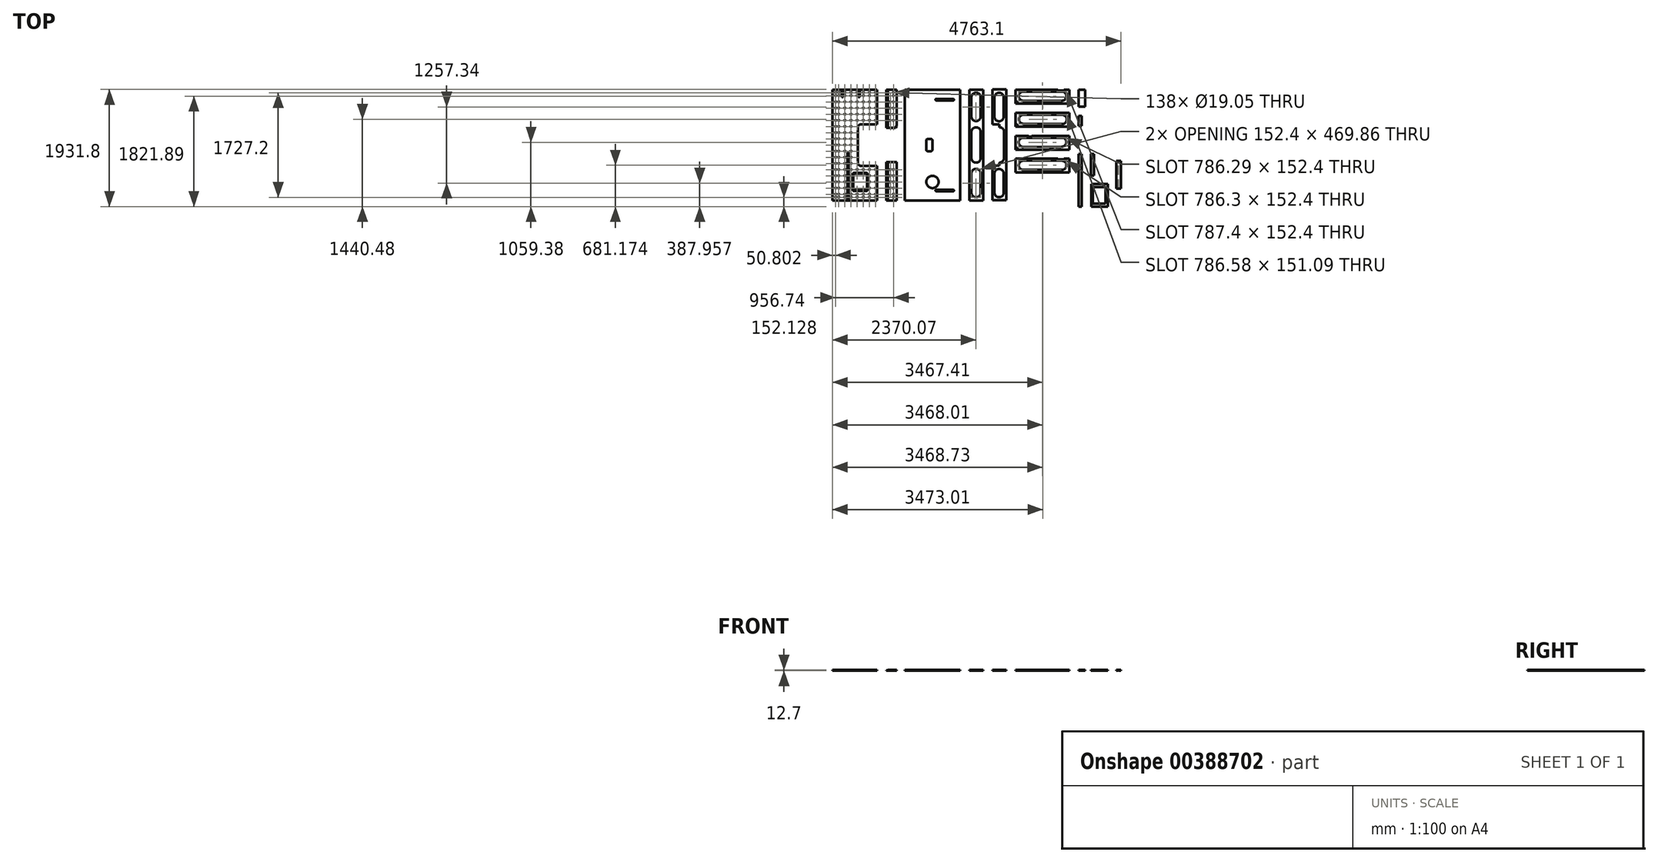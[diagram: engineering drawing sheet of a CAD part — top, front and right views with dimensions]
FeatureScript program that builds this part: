
annotation { "Feature Type Name" : "Feature", "Feature Type Description" : "" }
export const myFeature = defineFeature(function(context is Context, id is Id, definition is map)
    precondition{}
    {
        {
            var Q0;
            Q0=qCreatedBy(makeId("Top.planeOp"),FACE);
            var sketch = newSketch(context, id + "F0", { "sketchPlane" : qUnion([Q0])});
            skLineSegment(sketch, "E0", {"start": v(825, -153.67) * mm, "end": v(825, -725.17) * mm});
            skLineSegment(sketch, "E1", {"start": v(825, -725.17) * mm, "end": v(558.3, -725.17) * mm});
            skLineSegment(sketch, "E2", {"start": v(507.5, -775.97) * mm, "end": v(507.5, -1360.17) * mm});
            skLineSegment(sketch, "E3", {"start": v(558.3, -1410.97) * mm, "end": v(825, -1410.97) * mm});
            skLineSegment(sketch, "E4", {"start": v(825, -1410.97) * mm, "end": v(825, -1982.47) * mm});
            skLineSegment(sketch, "E5", {"start": v(88.4, -1982.47) * mm, "end": v(88.4, -153.67) * mm});
            skPoint(sketch, "E6.visualSharp", {"position": v(507.5, -725.17) * mm});
            skArc(sketch, "E6.filletArc", {"start": v(558.3, -725.17) * mm, "mid": v(522.37, -740.05) * mm, "end": v(507.5, -775.97) * mm});
            skPoint(sketch, "E7.visualSharp", {"position": v(507.5, -1410.97) * mm});
            skArc(sketch, "E7.filletArc", {"start": v(507.5, -1360.17) * mm, "mid": v(522.37, -1396.1) * mm, "end": v(558.3, -1410.97) * mm});
            skLineSegment(sketch, "E8", {"start": v(88.4, -153.67) * mm, "end": v(825, -153.67) * mm});
            skLineSegment(sketch, "E9", {"start": v(88.4, -1982.47) * mm, "end": v(825, -1982.47) * mm});
            skCircle(sketch, "E10", {"center": v(139.2, -1931.67) * mm, "radius": 9.53 * mm});
            skCircle(sketch, "E11.0.1.0", {"center": v(139.2, -1880.87) * mm, "radius": 9.53 * mm});
            skCircle(sketch, "E11.1.0.0", {"center": v(190, -1931.67) * mm, "radius": 9.53 * mm});
            skCircle(sketch, "E11.1.1.0", {"center": v(190, -1880.87) * mm, "radius": 9.53 * mm});
            skLineSegment(sketch, "E11.direction1", {"start": v(139.2, -1931.67) * mm, "end": v(190, -1931.67) * mm, "construction": true});
            skLineSegment(sketch, "E11.direction2", {"start": v(139.2, -1931.67) * mm, "end": v(139.2, -1880.87) * mm, "construction": true});
            skCircle(sketch, "E12", {"center": v(139.2, -1779.27) * mm, "radius": 9.53 * mm});
            skCircle(sketch, "E13.0.1.0", {"center": v(139.2, -1677.67) * mm, "radius": 9.53 * mm});
            skCircle(sketch, "E13.0.2.0", {"center": v(139.2, -1576.07) * mm, "radius": 9.53 * mm});
            skCircle(sketch, "E13.0.3.0", {"center": v(139.2, -1474.47) * mm, "radius": 9.53 * mm});
            skCircle(sketch, "E13.0.4.0", {"center": v(139.2, -1372.87) * mm, "radius": 9.53 * mm});
            skCircle(sketch, "E13.0.5.0", {"center": v(139.2, -1271.27) * mm, "radius": 9.53 * mm});
            skCircle(sketch, "E13.0.6.0", {"center": v(139.2, -1169.67) * mm, "radius": 9.53 * mm});
            skCircle(sketch, "E13.0.7.0", {"center": v(139.2, -1068.07) * mm, "radius": 9.53 * mm});
            skCircle(sketch, "E13.0.8.0", {"center": v(139.2, -966.47) * mm, "radius": 9.53 * mm});
            skCircle(sketch, "E13.0.9.0", {"center": v(139.2, -864.87) * mm, "radius": 9.53 * mm});
            skCircle(sketch, "E13.0.10.0", {"center": v(139.2, -763.27) * mm, "radius": 9.53 * mm});
            skCircle(sketch, "E13.0.11.0", {"center": v(139.2, -661.67) * mm, "radius": 9.53 * mm});
            skCircle(sketch, "E13.0.12.0", {"center": v(139.2, -560.07) * mm, "radius": 9.53 * mm});
            skCircle(sketch, "E13.0.13.0", {"center": v(139.2, -458.47) * mm, "radius": 9.53 * mm});
            skCircle(sketch, "E13.0.14.0", {"center": v(139.2, -356.87) * mm, "radius": 9.53 * mm});
            skCircle(sketch, "E13.1.0.0", {"center": v(190, -1779.27) * mm, "radius": 9.53 * mm});
            skCircle(sketch, "E13.1.1.0", {"center": v(190, -1677.67) * mm, "radius": 9.53 * mm});
            skCircle(sketch, "E13.1.2.0", {"center": v(190, -1576.07) * mm, "radius": 9.53 * mm});
            skCircle(sketch, "E13.1.3.0", {"center": v(190, -1474.47) * mm, "radius": 9.53 * mm});
            skCircle(sketch, "E13.1.4.0", {"center": v(190, -1372.87) * mm, "radius": 9.53 * mm});
            skCircle(sketch, "E13.1.5.0", {"center": v(190, -1271.27) * mm, "radius": 9.53 * mm});
            skCircle(sketch, "E13.1.6.0", {"center": v(190, -1169.67) * mm, "radius": 9.53 * mm});
            skCircle(sketch, "E13.1.7.0", {"center": v(190, -1068.07) * mm, "radius": 9.53 * mm});
            skCircle(sketch, "E13.1.8.0", {"center": v(190, -966.47) * mm, "radius": 9.53 * mm});
            skCircle(sketch, "E13.1.9.0", {"center": v(190, -864.87) * mm, "radius": 9.53 * mm});
            skCircle(sketch, "E13.1.10.0", {"center": v(190, -763.27) * mm, "radius": 9.53 * mm});
            skCircle(sketch, "E13.1.11.0", {"center": v(190, -661.67) * mm, "radius": 9.53 * mm});
            skCircle(sketch, "E13.1.12.0", {"center": v(190, -560.07) * mm, "radius": 9.53 * mm});
            skCircle(sketch, "E13.1.13.0", {"center": v(190, -458.47) * mm, "radius": 9.53 * mm});
            skCircle(sketch, "E13.1.14.0", {"center": v(190, -356.87) * mm, "radius": 9.53 * mm});
            skLineSegment(sketch, "E13.direction1", {"start": v(139.2, -1779.27) * mm, "end": v(190, -1779.27) * mm, "construction": true});
            skLineSegment(sketch, "E13.direction2", {"start": v(139.2, -1779.27) * mm, "end": v(139.2, -1677.67) * mm, "construction": true});
            skCircle(sketch, "E14.0.0.15", {"center": v(139.2, -255.27) * mm, "radius": 9.53 * mm});
            skCircle(sketch, "E14.0.1.15", {"center": v(190, -255.27) * mm, "radius": 9.53 * mm});
            skCircle(sketch, "E15", {"center": v(139.2, -204.47) * mm, "radius": 9.53 * mm});
            skCircle(sketch, "E16", {"center": v(190, -204.47) * mm, "radius": 9.53 * mm});
            skCircle(sketch, "E17", {"center": v(291.6, -1931.67) * mm, "radius": 9.53 * mm});
            skCircle(sketch, "E18.1.0.0", {"center": v(393.2, -1931.67) * mm, "radius": 9.53 * mm});
            skCircle(sketch, "E18.2.0.0", {"center": v(494.8, -1931.67) * mm, "radius": 9.53 * mm});
            skCircle(sketch, "E18.3.0.0", {"center": v(596.4, -1931.67) * mm, "radius": 9.53 * mm});
            skCircle(sketch, "E18.4.0.0", {"center": v(698, -1931.67) * mm, "radius": 9.53 * mm});
            skCircle(sketch, "E18.5.0.0", {"center": v(799.6, -1931.67) * mm, "radius": 9.53 * mm});
            skLineSegment(sketch, "E18.direction1", {"start": v(291.6, -1931.67) * mm, "end": v(393.2, -1931.67) * mm, "construction": true});
            skCircle(sketch, "E19", {"center": v(291.6, -1880.87) * mm, "radius": 9.53 * mm});
            skCircle(sketch, "E20.0.1.0", {"center": v(291.6, -1779.27) * mm, "radius": 9.53 * mm});
            skCircle(sketch, "E20.0.2.0", {"center": v(291.6, -1677.67) * mm, "radius": 9.53 * mm});
            skCircle(sketch, "E20.0.3.0", {"center": v(291.6, -1576.07) * mm, "radius": 9.53 * mm});
            skCircle(sketch, "E20.0.4.0", {"center": v(291.6, -1474.47) * mm, "radius": 9.53 * mm});
            skCircle(sketch, "E20.0.5.0", {"center": v(291.6, -1372.87) * mm, "radius": 9.53 * mm});
            skCircle(sketch, "E20.0.6.0", {"center": v(291.6, -1271.27) * mm, "radius": 9.53 * mm});
            skCircle(sketch, "E20.0.7.0", {"center": v(291.6, -1169.67) * mm, "radius": 9.53 * mm});
            skCircle(sketch, "E20.0.8.0", {"center": v(291.6, -1068.07) * mm, "radius": 9.53 * mm});
            skCircle(sketch, "E20.0.9.0", {"center": v(291.6, -966.47) * mm, "radius": 9.53 * mm});
            skCircle(sketch, "E20.0.10.0", {"center": v(291.6, -864.87) * mm, "radius": 9.53 * mm});
            skCircle(sketch, "E20.0.11.0", {"center": v(291.6, -763.27) * mm, "radius": 9.53 * mm});
            skCircle(sketch, "E20.0.12.0", {"center": v(291.6, -661.67) * mm, "radius": 9.53 * mm});
            skCircle(sketch, "E20.0.13.0", {"center": v(291.6, -560.07) * mm, "radius": 9.53 * mm});
            skCircle(sketch, "E20.0.14.0", {"center": v(291.6, -458.47) * mm, "radius": 9.53 * mm});
            skCircle(sketch, "E20.0.15.0", {"center": v(291.6, -356.87) * mm, "radius": 9.53 * mm});
            skCircle(sketch, "E20.1.1.0", {"center": v(393.2, -1779.27) * mm, "radius": 9.53 * mm});
            skCircle(sketch, "E20.1.2.0", {"center": v(393.2, -1677.67) * mm, "radius": 9.53 * mm});
            skCircle(sketch, "E20.1.3.0", {"center": v(393.2, -1576.07) * mm, "radius": 9.53 * mm});
            skCircle(sketch, "E20.1.4.0", {"center": v(393.2, -1474.47) * mm, "radius": 9.53 * mm});
            skCircle(sketch, "E20.1.5.0", {"center": v(393.2, -1372.87) * mm, "radius": 9.53 * mm});
            skCircle(sketch, "E20.1.6.0", {"center": v(393.2, -1271.27) * mm, "radius": 9.53 * mm});
            skCircle(sketch, "E20.1.7.0", {"center": v(393.2, -1169.67) * mm, "radius": 9.53 * mm});
            skCircle(sketch, "E20.1.8.0", {"center": v(393.2, -1068.07) * mm, "radius": 9.53 * mm});
            skCircle(sketch, "E20.1.9.0", {"center": v(393.2, -966.47) * mm, "radius": 9.53 * mm});
            skCircle(sketch, "E20.1.10.0", {"center": v(393.2, -864.87) * mm, "radius": 9.53 * mm});
            skCircle(sketch, "E20.1.11.0", {"center": v(393.2, -763.27) * mm, "radius": 9.53 * mm});
            skCircle(sketch, "E20.1.12.0", {"center": v(393.2, -661.67) * mm, "radius": 9.53 * mm});
            skCircle(sketch, "E20.1.13.0", {"center": v(393.2, -560.07) * mm, "radius": 9.53 * mm});
            skCircle(sketch, "E20.1.14.0", {"center": v(393.2, -458.47) * mm, "radius": 9.53 * mm});
            skCircle(sketch, "E20.1.15.0", {"center": v(393.2, -356.87) * mm, "radius": 9.53 * mm});
            skCircle(sketch, "E20.2.4.0", {"center": v(494.8, -1474.47) * mm, "radius": 9.53 * mm});
            skCircle(sketch, "E20.2.12.0", {"center": v(494.8, -661.67) * mm, "radius": 9.53 * mm});
            skCircle(sketch, "E20.2.13.0", {"center": v(494.8, -560.07) * mm, "radius": 9.53 * mm});
            skCircle(sketch, "E20.2.14.0", {"center": v(494.8, -458.47) * mm, "radius": 9.53 * mm});
            skCircle(sketch, "E20.2.15.0", {"center": v(494.8, -356.87) * mm, "radius": 9.53 * mm});
            skCircle(sketch, "E20.3.4.0", {"center": v(596.4, -1474.47) * mm, "radius": 9.53 * mm});
            skCircle(sketch, "E20.3.12.0", {"center": v(596.4, -661.67) * mm, "radius": 9.53 * mm});
            skCircle(sketch, "E20.3.13.0", {"center": v(596.4, -560.07) * mm, "radius": 9.53 * mm});
            skCircle(sketch, "E20.3.14.0", {"center": v(596.4, -458.47) * mm, "radius": 9.53 * mm});
            skCircle(sketch, "E20.3.15.0", {"center": v(596.4, -356.87) * mm, "radius": 9.53 * mm});
            skCircle(sketch, "E20.4.1.0", {"center": v(698, -1779.27) * mm, "radius": 9.53 * mm});
            skCircle(sketch, "E20.4.2.0", {"center": v(698, -1677.67) * mm, "radius": 9.53 * mm});
            skCircle(sketch, "E20.4.3.0", {"center": v(698, -1576.07) * mm, "radius": 9.53 * mm});
            skCircle(sketch, "E20.4.4.0", {"center": v(698, -1474.47) * mm, "radius": 9.53 * mm});
            skCircle(sketch, "E20.4.12.0", {"center": v(698, -661.67) * mm, "radius": 9.53 * mm});
            skCircle(sketch, "E20.4.13.0", {"center": v(698, -560.07) * mm, "radius": 9.53 * mm});
            skCircle(sketch, "E20.4.14.0", {"center": v(698, -458.47) * mm, "radius": 9.53 * mm});
            skCircle(sketch, "E20.4.15.0", {"center": v(698, -356.87) * mm, "radius": 9.53 * mm});
            skCircle(sketch, "E20.5.1.0", {"center": v(799.6, -1779.27) * mm, "radius": 9.53 * mm});
            skCircle(sketch, "E20.5.2.0", {"center": v(799.6, -1677.67) * mm, "radius": 9.53 * mm});
            skCircle(sketch, "E20.5.3.0", {"center": v(799.6, -1576.07) * mm, "radius": 9.53 * mm});
            skCircle(sketch, "E20.5.4.0", {"center": v(799.6, -1474.47) * mm, "radius": 9.53 * mm});
            skCircle(sketch, "E20.5.12.0", {"center": v(799.85, -661.67) * mm, "radius": 9.53 * mm});
            skCircle(sketch, "E20.5.13.0", {"center": v(799.6, -560.07) * mm, "radius": 9.53 * mm});
            skCircle(sketch, "E20.5.14.0", {"center": v(799.6, -458.47) * mm, "radius": 9.53 * mm});
            skCircle(sketch, "E20.5.15.0", {"center": v(799.6, -356.87) * mm, "radius": 9.53 * mm});
            skLineSegment(sketch, "E20.direction2", {"start": v(291.6, -1880.87) * mm, "end": v(291.6, -1779.27) * mm, "construction": true});
            skCircle(sketch, "E21.0.0.16", {"center": v(291.6, -255.27) * mm, "radius": 9.53 * mm});
            skCircle(sketch, "E21.0.1.16", {"center": v(393.2, -255.27) * mm, "radius": 9.53 * mm});
            skCircle(sketch, "E21.0.2.16", {"center": v(494.8, -255.27) * mm, "radius": 9.53 * mm});
            skCircle(sketch, "E21.0.3.16", {"center": v(596.4, -255.27) * mm, "radius": 9.53 * mm});
            skCircle(sketch, "E21.0.4.16", {"center": v(698, -255.27) * mm, "radius": 9.53 * mm});
            skCircle(sketch, "E21.0.5.16", {"center": v(799.6, -255.27) * mm, "radius": 9.53 * mm});
            skCircle(sketch, "E22", {"center": v(291.6, -204.47) * mm, "radius": 9.53 * mm});
            skCircle(sketch, "E23.1.0.0", {"center": v(393.2, -204.47) * mm, "radius": 9.53 * mm});
            skCircle(sketch, "E23.2.0.0", {"center": v(494.8, -204.47) * mm, "radius": 9.53 * mm});
            skCircle(sketch, "E23.3.0.0", {"center": v(596.4, -204.47) * mm, "radius": 9.53 * mm});
            skCircle(sketch, "E23.4.0.0", {"center": v(698, -204.47) * mm, "radius": 9.53 * mm});
            skCircle(sketch, "E23.5.0.0", {"center": v(799.6, -204.47) * mm, "radius": 9.53 * mm});
            skLineSegment(sketch, "E23.direction1", {"start": v(291.6, -204.47) * mm, "end": v(393.2, -204.47) * mm, "construction": true});
            skLineSegment(sketch, "E24.bottom", {"start": v(1281.72, -153.67) * mm, "end": v(2196.12, -153.67) * mm});
            skLineSegment(sketch, "E24.top", {"start": v(1281.72, -1982.47) * mm, "end": v(2196.12, -1982.47) * mm});
            skLineSegment(sketch, "E24.left", {"start": v(1281.72, -153.67) * mm, "end": v(1281.72, -1982.47) * mm});
            skLineSegment(sketch, "E24.right", {"start": v(2196.12, -153.67) * mm, "end": v(2196.12, -1982.47) * mm});
            skCircle(sketch, "E25", {"center": v(1738.92, -1677.67) * mm, "radius": 101.6 * mm});
            skLineSegment(sketch, "E26.bottom", {"start": v(1662.72, -966.47) * mm, "end": v(1713.52, -966.47) * mm});
            skLineSegment(sketch, "E26.top", {"start": v(1662.72, -1169.67) * mm, "end": v(1713.52, -1169.67) * mm});
            skLineSegment(sketch, "E26.left", {"start": v(1637.32, -991.87) * mm, "end": v(1637.32, -1144.27) * mm});
            skLineSegment(sketch, "E26.right", {"start": v(1738.92, -991.87) * mm, "end": v(1738.92, -1144.27) * mm});
            skLineSegment(sketch, "E27.bottom", {"start": v(1802.42, -306.07) * mm, "end": v(2081.82, -306.07) * mm});
            skLineSegment(sketch, "E27.top", {"start": v(1802.42, -331.47) * mm, "end": v(2081.82, -331.47) * mm});
            skArc(sketch, "E28", {"start": v(1802.42, -306.07) * mm, "mid": v(1789.72, -318.77) * mm, "end": v(1802.42, -331.47) * mm});
            skArc(sketch, "E29", {"start": v(2081.82, -331.47) * mm, "mid": v(2094.52, -318.77) * mm, "end": v(2081.82, -306.07) * mm});
            skLineSegment(sketch, "E30", {"start": v(1942.12, -306.07) * mm, "end": v(1942.12, -331.47) * mm, "construction": true});
            skLineSegment(sketch, "E31", {"start": v(1281.72, -1068.07) * mm, "end": v(2196.12, -1068.07) * mm, "construction": true});
            skLineSegment(sketch, "E32.MirrorCS", {"start": v(1802.42, -1830.07) * mm, "end": v(2081.82, -1830.07) * mm});
            skLineSegment(sketch, "E33.MirrorCS", {"start": v(1942.12, -1830.07) * mm, "end": v(1942.12, -1804.67) * mm, "construction": true});
            skArc(sketch, "E34.MirrorCS", {"start": v(2081.82, -1804.67) * mm, "mid": v(2094.52, -1817.37) * mm, "end": v(2081.82, -1830.07) * mm});
            skArc(sketch, "E35.MirrorCS", {"start": v(1802.42, -1830.07) * mm, "mid": v(1789.72, -1817.37) * mm, "end": v(1802.42, -1804.67) * mm});
            skLineSegment(sketch, "E36.MirrorCS", {"start": v(1802.42, -1804.67) * mm, "end": v(2081.82, -1804.67) * mm});
            skLineSegment(sketch, "E37", {"start": v(1688.12, -966.47) * mm, "end": v(1688.12, -1169.67) * mm, "construction": true});
            skLineSegment(sketch, "E38", {"start": v(1637.32, -1068.07) * mm, "end": v(1738.92, -1068.07) * mm, "construction": true});
            skPoint(sketch, "E39.visualSharp", {"position": v(1637.32, -966.47) * mm});
            skArc(sketch, "E39.filletArc", {"start": v(1662.72, -966.47) * mm, "mid": v(1644.76, -973.91) * mm, "end": v(1637.32, -991.87) * mm});
            skPoint(sketch, "E40.visualSharp", {"position": v(1738.92, -966.47) * mm});
            skArc(sketch, "E40.filletArc", {"start": v(1738.92, -991.87) * mm, "mid": v(1731.49, -973.91) * mm, "end": v(1713.52, -966.47) * mm});
            skPoint(sketch, "E41.visualSharp", {"position": v(1738.92, -1169.67) * mm});
            skArc(sketch, "E41.filletArc", {"start": v(1713.52, -1169.67) * mm, "mid": v(1731.49, -1162.23) * mm, "end": v(1738.92, -1144.27) * mm});
            skPoint(sketch, "E42.visualSharp", {"position": v(1637.32, -1169.67) * mm});
            skArc(sketch, "E42.filletArc", {"start": v(1637.32, -1144.27) * mm, "mid": v(1644.76, -1162.23) * mm, "end": v(1662.72, -1169.67) * mm});
            skLineSegment(sketch, "E43.bottom", {"start": v(2350.51, -152.77) * mm, "end": v(2579.11, -152.77) * mm});
            skLineSegment(sketch, "E43.top", {"start": v(2350.51, -1981.57) * mm, "end": v(2579.11, -1981.57) * mm});
            skLineSegment(sketch, "E43.left", {"start": v(2350.51, -152.77) * mm, "end": v(2350.51, -1981.57) * mm});
            skLineSegment(sketch, "E43.right", {"start": v(2579.11, -152.77) * mm, "end": v(2579.11, -1981.57) * mm});
            skLineSegment(sketch, "E44.bottom", {"start": v(2730.45, -152) * mm, "end": v(2959.05, -152) * mm});
            skLineSegment(sketch, "E44.top", {"start": v(2730.45, -1980.8) * mm, "end": v(2959.05, -1980.8) * mm});
            skLineSegment(sketch, "E44.left", {"start": v(2730.45, -152) * mm, "end": v(2730.45, -724.54) * mm});
            skLineSegment(sketch, "E44.right", {"start": v(2959.05, -152) * mm, "end": v(2959.05, -1980.8) * mm});
            skLineSegment(sketch, "E45.bottom", {"start": v(3111.9, -153.96) * mm, "end": v(3810.4, -153.96) * mm});
            skLineSegment(sketch, "E45.top", {"start": v(3111.9, -382.56) * mm, "end": v(4000.9, -382.56) * mm});
            skLineSegment(sketch, "E45.left", {"start": v(3111.9, -153.96) * mm, "end": v(3111.9, -382.56) * mm});
            skLineSegment(sketch, "E45.right", {"start": v(4000.9, -153.96) * mm, "end": v(4000.9, -382.56) * mm});
            skLineSegment(sketch, "E46", {"start": v(2350.51, -1067.17) * mm, "end": v(2989.6, -1067.17) * mm, "construction": true});
            skArc(sketch, "E47", {"start": v(2534.66, -279.77) * mm, "mid": v(2458.42, -203.57) * mm, "end": v(2382.26, -279.85) * mm});
            skArc(sketch, "E48", {"start": v(2382.43, -592.26) * mm, "mid": v(2455.96, -673.43) * mm, "end": v(2534.66, -597.27) * mm});
            skLineSegment(sketch, "E49", {"start": v(2534.66, -279.77) * mm, "end": v(2534.66, -597.27) * mm});
            skLineSegment(sketch, "E50", {"start": v(2382.26, -279.77) * mm, "end": v(2382.43, -602.36) * mm});
            skArc(sketch, "E51.MirrorCS", {"start": v(2534.66, -1854.57) * mm, "mid": v(2458.42, -1930.77) * mm, "end": v(2382.26, -1854.5) * mm});
            skLineSegment(sketch, "E52.MirrorCS", {"start": v(2534.66, -1854.57) * mm, "end": v(2534.66, -1537.07) * mm});
            skLineSegment(sketch, "E53.MirrorCS", {"start": v(2382.26, -1854.57) * mm, "end": v(2382.43, -1531.98) * mm});
            skArc(sketch, "E54.MirrorCS", {"start": v(2382.43, -1542.08) * mm, "mid": v(2455.96, -1460.91) * mm, "end": v(2534.66, -1537.07) * mm});
            skArc(sketch, "E55", {"start": v(2534.66, -851.27) * mm, "mid": v(2458.46, -775.07) * mm, "end": v(2382.26, -851.27) * mm});
            skArc(sketch, "E56", {"start": v(2382.26, -1283.07) * mm, "mid": v(2458.46, -1359.27) * mm, "end": v(2534.66, -1283.07) * mm});
            skLineSegment(sketch, "E57", {"start": v(2382.26, -851.27) * mm, "end": v(2382.26, -1283.07) * mm});
            skLineSegment(sketch, "E58", {"start": v(2534.66, -851.27) * mm, "end": v(2534.66, -1283.07) * mm});
            skLineSegment(sketch, "E59", {"start": v(2730.45, -724.54) * mm, "end": v(2844.75, -724.54) * mm});
            skLineSegment(sketch, "E60", {"start": v(2844.75, -724.54) * mm, "end": v(2844.75, -775.34) * mm});
            skLineSegment(sketch, "E61", {"start": v(2730.45, -1405.9) * mm, "end": v(2844.75, -1405.9) * mm});
            skLineSegment(sketch, "E62", {"start": v(2844.75, -1405.9) * mm, "end": v(2844.75, -1359) * mm});
            skPoint(sketch, "E62.endSnap0", {"position": v(2844.75, -1359) * mm});
            skLineSegment(sketch, "E63.trimOffspring", {"start": v(2730.45, -1405.9) * mm, "end": v(2730.45, -1980.8) * mm});
            skArc(sketch, "E64", {"start": v(3238.9, -185.71) * mm, "mid": v(3162.7, -261.91) * mm, "end": v(3238.9, -338.11) * mm});
            skArc(sketch, "E65", {"start": v(3873.9, -338.11) * mm, "mid": v(3950.1, -261.91) * mm, "end": v(3873.9, -185.71) * mm});
            skLineSegment(sketch, "E66", {"start": v(3238.9, -185.71) * mm, "end": v(3873.9, -185.71) * mm});
            skLineSegment(sketch, "E67", {"start": v(3238.9, -338.11) * mm, "end": v(3873.9, -338.11) * mm});
            skCircle(sketch, "E68", {"center": v(3129.36, -365.1) * mm, "radius": 15.88 * mm});
            skCircle(sketch, "E69", {"center": v(3704.04, -365.1) * mm, "radius": 15.88 * mm});
            skLineSegment(sketch, "E70.0.1.0", {"start": v(3111.87, -535.59) * mm, "end": v(3111.87, -764.19) * mm});
            skArc(sketch, "E70.0.1.1", {"start": v(3229.9, -567.77) * mm, "mid": v(3168.1, -649.73) * mm, "end": v(3243.98, -718.86) * mm});
            skLineSegment(sketch, "E70.0.1.2", {"start": v(4000.86, -538.84) * mm, "end": v(4000.67, -764.19) * mm});
            skArc(sketch, "E70.0.1.3", {"start": v(3904.38, -718.86) * mm, "mid": v(3952.62, -626.59) * mm, "end": v(3865.15, -570.1) * mm});
            skLineSegment(sketch, "E70.0.1.4", {"start": v(3243.98, -718.86) * mm, "end": v(3904.38, -718.86) * mm});
            skLineSegment(sketch, "E70.0.1.5", {"start": v(3229.9, -567.77) * mm, "end": v(3865.15, -570.1) * mm});
            skCircle(sketch, "E70.0.1.6", {"center": v(3704.04, -744.9) * mm, "radius": 15.88 * mm});
            skCircle(sketch, "E70.0.1.7", {"center": v(3129.36, -744.9) * mm, "radius": 15.88 * mm});
            skLineSegment(sketch, "E70.0.1.8", {"start": v(3111.87, -764.19) * mm, "end": v(4000.67, -764.19) * mm});
            skLineSegment(sketch, "E70.0.1.9", {"start": v(3111.87, -535.59) * mm, "end": v(4000.86, -538.84) * mm});
            skLineSegment(sketch, "E70.0.2.0", {"start": v(3111.85, -916.47) * mm, "end": v(3111.85, -1145.07) * mm});
            skArc(sketch, "E70.0.2.1", {"start": v(3238.85, -948.22) * mm, "mid": v(3162.65, -1024.42) * mm, "end": v(3238.85, -1100.62) * mm});
            skLineSegment(sketch, "E70.0.2.2", {"start": v(4000.85, -916.47) * mm, "end": v(4000.65, -1145.07) * mm});
            skArc(sketch, "E70.0.2.3", {"start": v(3873.84, -1096.26) * mm, "mid": v(3948.94, -1032.95) * mm, "end": v(3899.25, -948.22) * mm});
            skLineSegment(sketch, "E70.0.2.4", {"start": v(3238.85, -1100.62) * mm, "end": v(3873.84, -1096.26) * mm});
            skLineSegment(sketch, "E70.0.2.5", {"start": v(3238.85, -948.22) * mm, "end": v(3899.25, -948.22) * mm});
            skCircle(sketch, "E70.0.2.6", {"center": v(3704.04, -1125.58) * mm, "radius": 15.88 * mm});
            skCircle(sketch, "E70.0.2.7", {"center": v(3129.36, -1128.45) * mm, "radius": 15.88 * mm});
            skLineSegment(sketch, "E70.0.2.8", {"start": v(3111.85, -1145.07) * mm, "end": v(4000.65, -1145.07) * mm});
            skLineSegment(sketch, "E70.0.2.9", {"start": v(3111.85, -916.47) * mm, "end": v(3327.75, -916.47) * mm});
            skLineSegment(sketch, "E70.0.3.0", {"start": v(3113.17, -1294.68) * mm, "end": v(3113.17, -1523.28) * mm});
            skArc(sketch, "E70.0.3.1", {"start": v(3240.17, -1326.43) * mm, "mid": v(3163.97, -1402.63) * mm, "end": v(3240.17, -1478.83) * mm});
            skLineSegment(sketch, "E70.0.3.2", {"start": v(4001.97, -1294.68) * mm, "end": v(4001.97, -1523.28) * mm});
            skArc(sketch, "E70.0.3.3", {"start": v(3900.58, -1474.46) * mm, "mid": v(3950.27, -1389.73) * mm, "end": v(3875.17, -1326.43) * mm});
            skLineSegment(sketch, "E70.0.3.4", {"start": v(3240.17, -1478.83) * mm, "end": v(3900.58, -1474.46) * mm});
            skLineSegment(sketch, "E70.0.3.5", {"start": v(3240.17, -1326.43) * mm, "end": v(3875.17, -1326.43) * mm});
            skLineSegment(sketch, "E70.0.3.8", {"start": v(3113.17, -1523.28) * mm, "end": v(4001.97, -1523.28) * mm});
            skLineSegment(sketch, "E70.0.3.9", {"start": v(3113.17, -1294.68) * mm, "end": v(3811.47, -1294.68) * mm});
            skLineSegment(sketch, "E70.direction1", {"start": v(3111.9, -382.56) * mm, "end": v(3137.3, -382.56) * mm, "construction": true});
            skLineSegment(sketch, "E71", {"start": v(3810.4, -153.96) * mm, "end": v(3810.4, -166.66) * mm});
            skLineSegment(sketch, "E72", {"start": v(3810.4, -166.66) * mm, "end": v(3912, -166.66) * mm});
            skLineSegment(sketch, "E73", {"start": v(3912, -166.66) * mm, "end": v(3912, -153.96) * mm});
            skLineSegment(sketch, "E74.trimOffspring", {"start": v(3912, -153.96) * mm, "end": v(4000.9, -153.96) * mm});
            skLineSegment(sketch, "E75", {"start": v(3811.47, -1294.68) * mm, "end": v(3811.47, -1307.38) * mm});
            skLineSegment(sketch, "E76", {"start": v(3811.47, -1307.38) * mm, "end": v(3913.07, -1307.38) * mm});
            skLineSegment(sketch, "E77", {"start": v(3913.07, -1307.38) * mm, "end": v(3913.07, -1294.68) * mm});
            skLineSegment(sketch, "E78.trimOffspring", {"start": v(3913.07, -1294.68) * mm, "end": v(4001.97, -1294.68) * mm});
            skLineSegment(sketch, "E79", {"start": v(3327.75, -916.47) * mm, "end": v(3327.75, -932.32) * mm});
            skLineSegment(sketch, "E80", {"start": v(3327.75, -932.32) * mm, "end": v(3378.55, -932.32) * mm});
            skLineSegment(sketch, "E81", {"start": v(3378.55, -932.32) * mm, "end": v(3378.55, -916.47) * mm});
            skLineSegment(sketch, "E82.trimOffspring", {"start": v(3378.55, -916.47) * mm, "end": v(4000.85, -916.47) * mm});
            skCircle(sketch, "E83.1.0.0", {"center": v(393.2, -1880.87) * mm, "radius": 9.53 * mm});
            skCircle(sketch, "E83.2.0.0", {"center": v(494.8, -1880.87) * mm, "radius": 9.53 * mm});
            skCircle(sketch, "E83.3.0.0", {"center": v(596.4, -1880.87) * mm, "radius": 9.53 * mm});
            skCircle(sketch, "E83.4.0.0", {"center": v(698, -1880.87) * mm, "radius": 9.53 * mm});
            skCircle(sketch, "E83.5.0.0", {"center": v(799.6, -1880.87) * mm, "radius": 9.53 * mm});
            skLineSegment(sketch, "E83.direction1", {"start": v(291.6, -1880.87) * mm, "end": v(393.2, -1880.87) * mm, "construction": true});
            skLineSegment(sketch, "E84.bottom", {"start": v(978.46, -152.84) * mm, "end": v(1146.73, -152.84) * mm});
            skLineSegment(sketch, "E84.top", {"start": v(978.46, -784.67) * mm, "end": v(1127.3, -784.67) * mm});
            skLineSegment(sketch, "E84.left", {"start": v(978.46, -152.84) * mm, "end": v(978.46, -784.67) * mm});
            skLineSegment(sketch, "E84.right", {"start": v(1146.73, -152.84) * mm, "end": v(1146.73, -750.18) * mm});
            skLineSegment(sketch, "E85", {"start": v(1127.3, -784.67) * mm, "end": v(1146.73, -750.18) * mm});
            skCircle(sketch, "E86", {"center": v(1095.93, -661.67) * mm, "radius": 9.53 * mm});
            skCircle(sketch, "E87.0.1.0", {"center": v(1095.93, -560.07) * mm, "radius": 9.53 * mm});
            skCircle(sketch, "E87.0.2.0", {"center": v(1095.93, -458.47) * mm, "radius": 9.53 * mm});
            skCircle(sketch, "E87.0.3.0", {"center": v(1095.93, -356.87) * mm, "radius": 9.53 * mm});
            skCircle(sketch, "E87.0.4.0", {"center": v(1095.93, -255.27) * mm, "radius": 9.53 * mm});
            skCircle(sketch, "E87.1.0.0", {"center": v(1045.13, -661.67) * mm, "radius": 9.53 * mm});
            skCircle(sketch, "E87.1.1.0", {"center": v(1045.13, -560.07) * mm, "radius": 9.53 * mm});
            skCircle(sketch, "E87.1.2.0", {"center": v(1045.13, -458.47) * mm, "radius": 9.53 * mm});
            skCircle(sketch, "E87.1.3.0", {"center": v(1045.13, -356.87) * mm, "radius": 9.53 * mm});
            skLineSegment(sketch, "E87.direction1", {"start": v(1095.93, -661.67) * mm, "end": v(1045.13, -661.67) * mm, "construction": true});
            skLineSegment(sketch, "E87.direction2", {"start": v(1095.93, -661.67) * mm, "end": v(1095.93, -560.07) * mm, "construction": true});
            skCircle(sketch, "E88", {"center": v(1095.93, -204.47) * mm, "radius": 9.53 * mm});
            skLineSegment(sketch, "E89.bottom", {"start": v(978.46, -1350.13) * mm, "end": v(1146.73, -1350.13) * mm});
            skLineSegment(sketch, "E89.top", {"start": v(978.46, -1981.96) * mm, "end": v(1146.73, -1981.96) * mm});
            skLineSegment(sketch, "E89.left", {"start": v(978.46, -1350.13) * mm, "end": v(978.46, -1981.96) * mm});
            skLineSegment(sketch, "E89.right", {"start": v(1146.73, -1350.13) * mm, "end": v(1146.73, -1981.96) * mm});
            skCircle(sketch, "E90", {"center": v(1095.47, -1931.67) * mm, "radius": 9.53 * mm});
            skCircle(sketch, "E91", {"center": v(1095.47, -1880.87) * mm, "radius": 9.53 * mm});
            skCircle(sketch, "E92.0.1.0", {"center": v(1095.47, -1779.27) * mm, "radius": 9.53 * mm});
            skCircle(sketch, "E92.0.2.0", {"center": v(1095.47, -1677.67) * mm, "radius": 9.53 * mm});
            skCircle(sketch, "E92.0.3.0", {"center": v(1095.47, -1576.07) * mm, "radius": 9.53 * mm});
            skCircle(sketch, "E92.0.4.0", {"center": v(1095.47, -1474.47) * mm, "radius": 9.53 * mm});
            skCircle(sketch, "E92.1.1.0", {"center": v(1044.67, -1779.27) * mm, "radius": 9.53 * mm});
            skCircle(sketch, "E92.1.2.0", {"center": v(1044.67, -1677.67) * mm, "radius": 9.53 * mm});
            skCircle(sketch, "E92.1.3.0", {"center": v(1044.67, -1576.07) * mm, "radius": 9.53 * mm});
            skCircle(sketch, "E92.1.4.0", {"center": v(1044.67, -1474.47) * mm, "radius": 9.53 * mm});
            skLineSegment(sketch, "E92.direction1", {"start": v(1095.47, -1880.87) * mm, "end": v(1044.67, -1880.87) * mm, "construction": true});
            skLineSegment(sketch, "E92.direction2", {"start": v(1095.47, -1880.87) * mm, "end": v(1095.47, -1779.27) * mm, "construction": true});
            skLineSegment(sketch, "E93.bottom", {"start": v(4154.21, -152.37) * mm, "end": v(4262.16, -152.37) * mm});
            skLineSegment(sketch, "E93.top", {"start": v(4154.21, -431.77) * mm, "end": v(4262.16, -431.77) * mm});
            skLineSegment(sketch, "E93.left", {"start": v(4154.21, -152.37) * mm, "end": v(4154.21, -431.77) * mm});
            skLineSegment(sketch, "E93.right", {"start": v(4262.16, -152.37) * mm, "end": v(4262.16, -431.77) * mm});
            skLineSegment(sketch, "E94.bottom", {"start": v(4155.11, -584.67) * mm, "end": v(4205.91, -584.67) * mm});
            skLineSegment(sketch, "E94.top", {"start": v(4155.11, -752.95) * mm, "end": v(4205.91, -752.95) * mm});
            skLineSegment(sketch, "E94.left", {"start": v(4155.11, -584.67) * mm, "end": v(4155.11, -752.95) * mm});
            skLineSegment(sketch, "E94.right", {"start": v(4205.91, -584.67) * mm, "end": v(4205.91, -752.95) * mm});
            skLineSegment(sketch, "E95.bottom", {"start": v(4154.26, -1213.85) * mm, "end": v(4205.06, -1213.85) * mm});
            skLineSegment(sketch, "E95.top", {"start": v(4154.26, -2083.8) * mm, "end": v(4205.06, -2083.8) * mm});
            skLineSegment(sketch, "E95.left", {"start": v(4154.26, -1213.85) * mm, "end": v(4154.26, -2083.8) * mm});
            skLineSegment(sketch, "E95.right", {"start": v(4205.06, -1213.85) * mm, "end": v(4205.06, -2083.8) * mm});
            skLineSegment(sketch, "E96.bottom", {"start": v(4357.04, -1213.53) * mm, "end": v(4407.84, -1213.53) * mm});
            skLineSegment(sketch, "E96.top", {"start": v(4357.04, -1569.13) * mm, "end": v(4407.84, -1569.13) * mm});
            skLineSegment(sketch, "E96.left", {"start": v(4357.04, -1213.53) * mm, "end": v(4357.04, -1569.13) * mm});
            skLineSegment(sketch, "E96.right", {"start": v(4407.84, -1213.53) * mm, "end": v(4407.84, -1569.13) * mm});
            skLineSegment(sketch, "E97.bottom", {"start": v(4359.31, -1708.27) * mm, "end": v(4632.36, -1708.27) * mm});
            skLineSegment(sketch, "E97.top", {"start": v(4359.31, -2082.92) * mm, "end": v(4632.36, -2082.92) * mm});
            skLineSegment(sketch, "E97.left", {"start": v(4359.31, -1708.27) * mm, "end": v(4359.31, -2082.92) * mm});
            skLineSegment(sketch, "E97.right", {"start": v(4632.36, -1708.27) * mm, "end": v(4632.36, -2082.92) * mm});
            skLineSegment(sketch, "E98.bottom", {"start": v(4775.3, -1329.85) * mm, "end": v(4851.5, -1329.85) * mm});
            skLineSegment(sketch, "E98.top", {"start": v(4775.3, -1787.05) * mm, "end": v(4851.5, -1787.05) * mm});
            skLineSegment(sketch, "E98.left", {"start": v(4775.3, -1329.85) * mm, "end": v(4775.3, -1787.05) * mm});
            skLineSegment(sketch, "E98.right", {"start": v(4851.5, -1329.85) * mm, "end": v(4851.5, -1787.05) * mm});
            skLineSegment(sketch, "E99", {"start": v(2579.11, -152.77) * mm, "end": v(2730.45, -152) * mm, "construction": true});
            skArc(sketch, "E100.MirrorCS", {"start": v(2763.05, -274.59) * mm, "mid": v(2839.22, -205.87) * mm, "end": v(2915.37, -274.6) * mm});
            skLineSegment(sketch, "E101.MirrorCS", {"start": v(2763.05, -274.59) * mm, "end": v(2763.05, -605.46) * mm});
            skLineSegment(sketch, "E102.MirrorCS", {"start": v(2915.37, -274.6) * mm, "end": v(2915.2, -599.5) * mm});
            skArc(sketch, "E103.MirrorCS", {"start": v(2915.2, -599.5) * mm, "mid": v(2841.99, -675.48) * mm, "end": v(2763.05, -605.46) * mm});
            skArc(sketch, "E104.MirrorCS", {"start": v(2844.75, -775.34) * mm, "mid": v(2899.74, -795.91) * mm, "end": v(2920.42, -850.87) * mm});
            skLineSegment(sketch, "E105.MirrorCS", {"start": v(2920.42, -850.87) * mm, "end": v(2920.42, -1282.67) * mm});
            skArc(sketch, "E106.MirrorCS", {"start": v(2920.42, -1282.67) * mm, "mid": v(2897, -1335.12) * mm, "end": v(2844.75, -1359) * mm});
            skArc(sketch, "E107.MirrorCS", {"start": v(2914.88, -1546.84) * mm, "mid": v(2839, -1464.04) * mm, "end": v(2763.05, -1546.76) * mm});
            skLineSegment(sketch, "E108.MirrorCS", {"start": v(2763.05, -1855.3) * mm, "end": v(2763.05, -1546.76) * mm});
            skLineSegment(sketch, "E109.MirrorCS", {"start": v(2915.04, -1852.68) * mm, "end": v(2914.88, -1546.84) * mm});
            skArc(sketch, "E110.MirrorCS", {"start": v(2763.05, -1855.3) * mm, "mid": v(2840.36, -1929.99) * mm, "end": v(2915.04, -1852.68) * mm});
            skPoint(sketch, "E111.orphan", {"position": v(2774.9, -851.27) * mm});
            skPoint(sketch, "E112.orphan", {"position": v(2778.88, -851.83) * mm});
            skPoint(sketch, "E113.MirrorCS.end.orphan", {"position": v(2774.9, -1283.07) * mm});
            skPoint(sketch, "E114.orphan", {"position": v(2758.2, -1284.42) * mm});
            skSolve(sketch);
        }
        {
            var Q0;
            Q0 = qSketchRegion(id + "F0", true);
            extrude(context, id + "F1", {"entities" : qUnion([Q0]), "depth" : 12.7 * mm});
        }
        {
            var Q0;
            Q0=makeQuery(id+"F1.opExtrude","CAP_FACE",FACE,{"disambiguationData":[OSD([sQuery(id+"F0.wireOp",EDGE,"E0"),sQuery(id+"F0.wireOp",EDGE,"E1"),sQuery(id+"F0.wireOp",EDGE,"E2"),sQuery(id+"F0.wireOp",EDGE,"E3"),sQuery(id+"F0.wireOp",EDGE,"E4"),sQuery(id+"F0.wireOp",EDGE,"E5"),sQuery(id+"F0.wireOp",EDGE,"E6.filletArc"),sQuery(id+"F0.wireOp",EDGE,"E7.filletArc"),sQuery(id+"F0.wireOp",EDGE,"E8"),sQuery(id+"F0.wireOp",EDGE,"E9"),sQuery(id+"F0.wireOp",EDGE,"E10"),sQuery(id+"F0.wireOp",EDGE,"E11.0.1.0"),sQuery(id+"F0.wireOp",EDGE,"E11.1.0.0"),sQuery(id+"F0.wireOp",EDGE,"E11.1.1.0"),sQuery(id+"F0.wireOp",EDGE,"E12"),sQuery(id+"F0.wireOp",EDGE,"E13.0.1.0"),sQuery(id+"F0.wireOp",EDGE,"E13.0.2.0"),sQuery(id+"F0.wireOp",EDGE,"E13.0.3.0"),sQuery(id+"F0.wireOp",EDGE,"E13.0.4.0"),sQuery(id+"F0.wireOp",EDGE,"E13.0.5.0"),sQuery(id+"F0.wireOp",EDGE,"E13.0.6.0"),sQuery(id+"F0.wireOp",EDGE,"E13.0.7.0"),sQuery(id+"F0.wireOp",EDGE,"E13.0.8.0"),sQuery(id+"F0.wireOp",EDGE,"E13.0.9.0"),sQuery(id+"F0.wireOp",EDGE,"E13.0.10.0"),sQuery(id+"F0.wireOp",EDGE,"E13.0.11.0"),sQuery(id+"F0.wireOp",EDGE,"E13.0.12.0"),sQuery(id+"F0.wireOp",EDGE,"E13.0.13.0"),sQuery(id+"F0.wireOp",EDGE,"E13.0.14.0"),sQuery(id+"F0.wireOp",EDGE,"E13.1.0.0"),sQuery(id+"F0.wireOp",EDGE,"E13.1.1.0"),sQuery(id+"F0.wireOp",EDGE,"E13.1.2.0"),sQuery(id+"F0.wireOp",EDGE,"E13.1.3.0"),sQuery(id+"F0.wireOp",EDGE,"E13.1.4.0"),sQuery(id+"F0.wireOp",EDGE,"E13.1.5.0"),sQuery(id+"F0.wireOp",EDGE,"E13.1.6.0"),sQuery(id+"F0.wireOp",EDGE,"E13.1.7.0"),sQuery(id+"F0.wireOp",EDGE,"E13.1.8.0"),sQuery(id+"F0.wireOp",EDGE,"E13.1.9.0"),sQuery(id+"F0.wireOp",EDGE,"E13.1.10.0"),sQuery(id+"F0.wireOp",EDGE,"E13.1.11.0"),sQuery(id+"F0.wireOp",EDGE,"E13.1.12.0"),sQuery(id+"F0.wireOp",EDGE,"E13.1.13.0"),sQuery(id+"F0.wireOp",EDGE,"E13.1.14.0"),sQuery(id+"F0.wireOp",EDGE,"E14.0.0.15"),sQuery(id+"F0.wireOp",EDGE,"E14.0.1.15"),sQuery(id+"F0.wireOp",EDGE,"E15"),sQuery(id+"F0.wireOp",EDGE,"E16"),sQuery(id+"F0.wireOp",EDGE,"E17"),sQuery(id+"F0.wireOp",EDGE,"E18.1.0.0"),sQuery(id+"F0.wireOp",EDGE,"E18.2.0.0"),sQuery(id+"F0.wireOp",EDGE,"E18.3.0.0"),sQuery(id+"F0.wireOp",EDGE,"E18.4.0.0"),sQuery(id+"F0.wireOp",EDGE,"E18.5.0.0"),sQuery(id+"F0.wireOp",EDGE,"E19"),sQuery(id+"F0.wireOp",EDGE,"E20.0.1.0"),sQuery(id+"F0.wireOp",EDGE,"E20.0.2.0"),sQuery(id+"F0.wireOp",EDGE,"E20.0.3.0"),sQuery(id+"F0.wireOp",EDGE,"E20.0.4.0"),sQuery(id+"F0.wireOp",EDGE,"E20.0.5.0"),sQuery(id+"F0.wireOp",EDGE,"E20.0.6.0"),sQuery(id+"F0.wireOp",EDGE,"E20.0.7.0"),sQuery(id+"F0.wireOp",EDGE,"E20.0.8.0"),sQuery(id+"F0.wireOp",EDGE,"E20.0.9.0"),sQuery(id+"F0.wireOp",EDGE,"E20.0.10.0"),sQuery(id+"F0.wireOp",EDGE,"E20.0.11.0"),sQuery(id+"F0.wireOp",EDGE,"E20.0.12.0"),sQuery(id+"F0.wireOp",EDGE,"E20.0.13.0"),sQuery(id+"F0.wireOp",EDGE,"E20.0.14.0"),sQuery(id+"F0.wireOp",EDGE,"E20.0.15.0"),sQuery(id+"F0.wireOp",EDGE,"E20.1.0.0"),sQuery(id+"F0.wireOp",EDGE,"E20.1.1.0"),sQuery(id+"F0.wireOp",EDGE,"E20.1.2.0"),sQuery(id+"F0.wireOp",EDGE,"E20.1.3.0"),sQuery(id+"F0.wireOp",EDGE,"E20.1.4.0"),sQuery(id+"F0.wireOp",EDGE,"E20.1.5.0"),sQuery(id+"F0.wireOp",EDGE,"E20.1.6.0"),sQuery(id+"F0.wireOp",EDGE,"E20.1.7.0"),sQuery(id+"F0.wireOp",EDGE,"E20.1.8.0"),sQuery(id+"F0.wireOp",EDGE,"E20.1.9.0"),sQuery(id+"F0.wireOp",EDGE,"E20.1.10.0"),sQuery(id+"F0.wireOp",EDGE,"E20.1.11.0"),sQuery(id+"F0.wireOp",EDGE,"E20.1.12.0"),sQuery(id+"F0.wireOp",EDGE,"E20.1.13.0"),sQuery(id+"F0.wireOp",EDGE,"E20.1.14.0"),sQuery(id+"F0.wireOp",EDGE,"E20.1.15.0"),sQuery(id+"F0.wireOp",EDGE,"E20.2.0.0"),sQuery(id+"F0.wireOp",EDGE,"E20.2.1.0"),sQuery(id+"F0.wireOp",EDGE,"E20.2.2.0"),sQuery(id+"F0.wireOp",EDGE,"E20.2.3.0"),sQuery(id+"F0.wireOp",EDGE,"E20.2.4.0"),sQuery(id+"F0.wireOp",EDGE,"E20.2.12.0"),sQuery(id+"F0.wireOp",EDGE,"E20.2.13.0"),sQuery(id+"F0.wireOp",EDGE,"E20.2.14.0"),sQuery(id+"F0.wireOp",EDGE,"E20.2.15.0"),sQuery(id+"F0.wireOp",EDGE,"E20.3.0.0"),sQuery(id+"F0.wireOp",EDGE,"E20.3.1.0"),sQuery(id+"F0.wireOp",EDGE,"E20.3.2.0"),sQuery(id+"F0.wireOp",EDGE,"E20.3.3.0"),sQuery(id+"F0.wireOp",EDGE,"E20.3.4.0"),sQuery(id+"F0.wireOp",EDGE,"E20.3.12.0"),sQuery(id+"F0.wireOp",EDGE,"E20.3.13.0"),sQuery(id+"F0.wireOp",EDGE,"E20.3.14.0"),sQuery(id+"F0.wireOp",EDGE,"E20.3.15.0"),sQuery(id+"F0.wireOp",EDGE,"E20.4.0.0"),sQuery(id+"F0.wireOp",EDGE,"E20.4.1.0"),sQuery(id+"F0.wireOp",EDGE,"E20.4.2.0"),sQuery(id+"F0.wireOp",EDGE,"E20.4.3.0"),sQuery(id+"F0.wireOp",EDGE,"E20.4.4.0"),sQuery(id+"F0.wireOp",EDGE,"E20.4.12.0"),sQuery(id+"F0.wireOp",EDGE,"E20.4.13.0"),sQuery(id+"F0.wireOp",EDGE,"E20.4.14.0"),sQuery(id+"F0.wireOp",EDGE,"E20.4.15.0"),sQuery(id+"F0.wireOp",EDGE,"E20.5.0.0"),sQuery(id+"F0.wireOp",EDGE,"E20.5.1.0"),sQuery(id+"F0.wireOp",EDGE,"E20.5.2.0"),sQuery(id+"F0.wireOp",EDGE,"E20.5.3.0"),sQuery(id+"F0.wireOp",EDGE,"E20.5.4.0"),sQuery(id+"F0.wireOp",EDGE,"E20.5.12.0"),sQuery(id+"F0.wireOp",EDGE,"E20.5.13.0"),sQuery(id+"F0.wireOp",EDGE,"E20.5.14.0"),sQuery(id+"F0.wireOp",EDGE,"E20.5.15.0"),sQuery(id+"F0.wireOp",EDGE,"E21.0.0.16"),sQuery(id+"F0.wireOp",EDGE,"E21.0.1.16"),sQuery(id+"F0.wireOp",EDGE,"E21.0.2.16"),sQuery(id+"F0.wireOp",EDGE,"E21.0.3.16"),sQuery(id+"F0.wireOp",EDGE,"E21.0.4.16"),sQuery(id+"F0.wireOp",EDGE,"E21.0.5.16"),sQuery(id+"F0.wireOp",EDGE,"E22"),sQuery(id+"F0.wireOp",EDGE,"E23.1.0.0"),sQuery(id+"F0.wireOp",EDGE,"E23.2.0.0"),sQuery(id+"F0.wireOp",EDGE,"E23.3.0.0"),sQuery(id+"F0.wireOp",EDGE,"E23.4.0.0"),sQuery(id+"F0.wireOp",EDGE,"E23.5.0.0")])],"isStart":false});
            var sketch = newSketch(context, id + "F2", { "sketchPlane" : qUnion([Q0])});
            skLineSegment(sketch, "E115", {"start": v(240.8, -153.67) * mm, "end": v(240.8, -274.03) * mm});
            skLineSegment(sketch, "E116", {"start": v(240.8, -274.03) * mm, "end": v(266.2, -274.03) * mm});
            skLineSegment(sketch, "E117", {"start": v(266.2, -274.03) * mm, "end": v(266.2, -153.67) * mm});
            skLineSegment(sketch, "E118", {"start": v(266.2, -153.67) * mm, "end": v(240.8, -153.67) * mm});
            skLineSegment(sketch, "E119.bottom", {"start": v(510.67, -153.67) * mm, "end": v(536.07, -153.67) * mm});
            skLineSegment(sketch, "E119.top", {"start": v(510.67, -274.03) * mm, "end": v(536.07, -274.03) * mm});
            skLineSegment(sketch, "E119.left", {"start": v(510.67, -153.67) * mm, "end": v(510.67, -274.03) * mm});
            skLineSegment(sketch, "E119.right", {"start": v(536.07, -153.67) * mm, "end": v(536.07, -274.03) * mm});
            skLineSegment(sketch, "E120.bottom", {"start": v(332.87, -1982.47) * mm, "end": v(351.92, -1982.47) * mm});
            skLineSegment(sketch, "E120.top", {"start": v(332.87, -1188.89) * mm, "end": v(351.92, -1188.89) * mm});
            skLineSegment(sketch, "E120.left", {"start": v(332.87, -1982.47) * mm, "end": v(332.87, -1188.89) * mm});
            skLineSegment(sketch, "E120.right", {"start": v(351.92, -1982.47) * mm, "end": v(351.92, -1188.89) * mm});
            skLineSegment(sketch, "E121", {"start": v(253.5, -153.67) * mm, "end": v(253.5, -274.03) * mm, "construction": true});
            skLineSegment(sketch, "E122", {"start": v(523.37, -153.67) * mm, "end": v(523.37, -274.03) * mm, "construction": true});
            skLineSegment(sketch, "E123", {"start": v(342.4, -1188.89) * mm, "end": v(342.4, -1982.47) * mm, "construction": true});
            skSolve(sketch);
        }
        {
            var Q0;
            Q0 = qSketchRegion(id + "F2", true);
            extrude(context, id + "F3", {"entities" : qUnion([Q0]), "operationType" : NewBodyOperationType.REMOVE, "oppositeDirection" : true, "depth" : 9.52 * mm});
        }
        {
            var Q0;
            Q0=makeQuery(id+"F1.opExtrude","CAP_FACE",FACE,{"disambiguationData":[OSD([sQuery(id+"F0.wireOp",EDGE,"E0"),sQuery(id+"F0.wireOp",EDGE,"E1"),sQuery(id+"F0.wireOp",EDGE,"E2"),sQuery(id+"F0.wireOp",EDGE,"E3"),sQuery(id+"F0.wireOp",EDGE,"E4"),sQuery(id+"F0.wireOp",EDGE,"E5"),sQuery(id+"F0.wireOp",EDGE,"E6.filletArc"),sQuery(id+"F0.wireOp",EDGE,"E7.filletArc"),sQuery(id+"F0.wireOp",EDGE,"E8"),sQuery(id+"F0.wireOp",EDGE,"E9"),sQuery(id+"F0.wireOp",EDGE,"E10"),sQuery(id+"F0.wireOp",EDGE,"E11.0.1.0"),sQuery(id+"F0.wireOp",EDGE,"E11.1.0.0"),sQuery(id+"F0.wireOp",EDGE,"E11.1.1.0"),sQuery(id+"F0.wireOp",EDGE,"E12"),sQuery(id+"F0.wireOp",EDGE,"E13.0.1.0"),sQuery(id+"F0.wireOp",EDGE,"E13.0.2.0"),sQuery(id+"F0.wireOp",EDGE,"E13.0.3.0"),sQuery(id+"F0.wireOp",EDGE,"E13.0.4.0"),sQuery(id+"F0.wireOp",EDGE,"E13.0.5.0"),sQuery(id+"F0.wireOp",EDGE,"E13.0.6.0"),sQuery(id+"F0.wireOp",EDGE,"E13.0.7.0"),sQuery(id+"F0.wireOp",EDGE,"E13.0.8.0"),sQuery(id+"F0.wireOp",EDGE,"E13.0.9.0"),sQuery(id+"F0.wireOp",EDGE,"E13.0.10.0"),sQuery(id+"F0.wireOp",EDGE,"E13.0.11.0"),sQuery(id+"F0.wireOp",EDGE,"E13.0.12.0"),sQuery(id+"F0.wireOp",EDGE,"E13.0.13.0"),sQuery(id+"F0.wireOp",EDGE,"E13.0.14.0"),sQuery(id+"F0.wireOp",EDGE,"E13.1.0.0"),sQuery(id+"F0.wireOp",EDGE,"E13.1.1.0"),sQuery(id+"F0.wireOp",EDGE,"E13.1.2.0"),sQuery(id+"F0.wireOp",EDGE,"E13.1.3.0"),sQuery(id+"F0.wireOp",EDGE,"E13.1.4.0"),sQuery(id+"F0.wireOp",EDGE,"E13.1.5.0"),sQuery(id+"F0.wireOp",EDGE,"E13.1.6.0"),sQuery(id+"F0.wireOp",EDGE,"E13.1.7.0"),sQuery(id+"F0.wireOp",EDGE,"E13.1.8.0"),sQuery(id+"F0.wireOp",EDGE,"E13.1.9.0"),sQuery(id+"F0.wireOp",EDGE,"E13.1.10.0"),sQuery(id+"F0.wireOp",EDGE,"E13.1.11.0"),sQuery(id+"F0.wireOp",EDGE,"E13.1.12.0"),sQuery(id+"F0.wireOp",EDGE,"E13.1.13.0"),sQuery(id+"F0.wireOp",EDGE,"E13.1.14.0"),sQuery(id+"F0.wireOp",EDGE,"E14.0.0.15"),sQuery(id+"F0.wireOp",EDGE,"E14.0.1.15"),sQuery(id+"F0.wireOp",EDGE,"E15"),sQuery(id+"F0.wireOp",EDGE,"E16"),sQuery(id+"F0.wireOp",EDGE,"E17"),sQuery(id+"F0.wireOp",EDGE,"E18.1.0.0"),sQuery(id+"F0.wireOp",EDGE,"E18.2.0.0"),sQuery(id+"F0.wireOp",EDGE,"E18.3.0.0"),sQuery(id+"F0.wireOp",EDGE,"E18.4.0.0"),sQuery(id+"F0.wireOp",EDGE,"E18.5.0.0"),sQuery(id+"F0.wireOp",EDGE,"E19"),sQuery(id+"F0.wireOp",EDGE,"E20.0.1.0"),sQuery(id+"F0.wireOp",EDGE,"E20.0.2.0"),sQuery(id+"F0.wireOp",EDGE,"E20.0.3.0"),sQuery(id+"F0.wireOp",EDGE,"E20.0.4.0"),sQuery(id+"F0.wireOp",EDGE,"E20.0.5.0"),sQuery(id+"F0.wireOp",EDGE,"E20.0.6.0"),sQuery(id+"F0.wireOp",EDGE,"E20.0.7.0"),sQuery(id+"F0.wireOp",EDGE,"E20.0.8.0"),sQuery(id+"F0.wireOp",EDGE,"E20.0.9.0"),sQuery(id+"F0.wireOp",EDGE,"E20.0.10.0"),sQuery(id+"F0.wireOp",EDGE,"E20.0.11.0"),sQuery(id+"F0.wireOp",EDGE,"E20.0.12.0"),sQuery(id+"F0.wireOp",EDGE,"E20.0.13.0"),sQuery(id+"F0.wireOp",EDGE,"E20.0.14.0"),sQuery(id+"F0.wireOp",EDGE,"E20.0.15.0"),sQuery(id+"F0.wireOp",EDGE,"E20.1.0.0"),sQuery(id+"F0.wireOp",EDGE,"E20.1.1.0"),sQuery(id+"F0.wireOp",EDGE,"E20.1.2.0"),sQuery(id+"F0.wireOp",EDGE,"E20.1.3.0"),sQuery(id+"F0.wireOp",EDGE,"E20.1.4.0"),sQuery(id+"F0.wireOp",EDGE,"E20.1.5.0"),sQuery(id+"F0.wireOp",EDGE,"E20.1.6.0"),sQuery(id+"F0.wireOp",EDGE,"E20.1.7.0"),sQuery(id+"F0.wireOp",EDGE,"E20.1.8.0"),sQuery(id+"F0.wireOp",EDGE,"E20.1.9.0"),sQuery(id+"F0.wireOp",EDGE,"E20.1.10.0"),sQuery(id+"F0.wireOp",EDGE,"E20.1.11.0"),sQuery(id+"F0.wireOp",EDGE,"E20.1.12.0"),sQuery(id+"F0.wireOp",EDGE,"E20.1.13.0"),sQuery(id+"F0.wireOp",EDGE,"E20.1.14.0"),sQuery(id+"F0.wireOp",EDGE,"E20.1.15.0"),sQuery(id+"F0.wireOp",EDGE,"E20.2.0.0"),sQuery(id+"F0.wireOp",EDGE,"E20.2.1.0"),sQuery(id+"F0.wireOp",EDGE,"E20.2.2.0"),sQuery(id+"F0.wireOp",EDGE,"E20.2.3.0"),sQuery(id+"F0.wireOp",EDGE,"E20.2.4.0"),sQuery(id+"F0.wireOp",EDGE,"E20.2.12.0"),sQuery(id+"F0.wireOp",EDGE,"E20.2.13.0"),sQuery(id+"F0.wireOp",EDGE,"E20.2.14.0"),sQuery(id+"F0.wireOp",EDGE,"E20.2.15.0"),sQuery(id+"F0.wireOp",EDGE,"E20.3.0.0"),sQuery(id+"F0.wireOp",EDGE,"E20.3.1.0"),sQuery(id+"F0.wireOp",EDGE,"E20.3.2.0"),sQuery(id+"F0.wireOp",EDGE,"E20.3.3.0"),sQuery(id+"F0.wireOp",EDGE,"E20.3.4.0"),sQuery(id+"F0.wireOp",EDGE,"E20.3.12.0"),sQuery(id+"F0.wireOp",EDGE,"E20.3.13.0"),sQuery(id+"F0.wireOp",EDGE,"E20.3.14.0"),sQuery(id+"F0.wireOp",EDGE,"E20.3.15.0"),sQuery(id+"F0.wireOp",EDGE,"E20.4.0.0"),sQuery(id+"F0.wireOp",EDGE,"E20.4.1.0"),sQuery(id+"F0.wireOp",EDGE,"E20.4.2.0"),sQuery(id+"F0.wireOp",EDGE,"E20.4.3.0"),sQuery(id+"F0.wireOp",EDGE,"E20.4.4.0"),sQuery(id+"F0.wireOp",EDGE,"E20.4.12.0"),sQuery(id+"F0.wireOp",EDGE,"E20.4.13.0"),sQuery(id+"F0.wireOp",EDGE,"E20.4.14.0"),sQuery(id+"F0.wireOp",EDGE,"E20.4.15.0"),sQuery(id+"F0.wireOp",EDGE,"E20.5.0.0"),sQuery(id+"F0.wireOp",EDGE,"E20.5.1.0"),sQuery(id+"F0.wireOp",EDGE,"E20.5.2.0"),sQuery(id+"F0.wireOp",EDGE,"E20.5.3.0"),sQuery(id+"F0.wireOp",EDGE,"E20.5.4.0"),sQuery(id+"F0.wireOp",EDGE,"E20.5.12.0"),sQuery(id+"F0.wireOp",EDGE,"E20.5.13.0"),sQuery(id+"F0.wireOp",EDGE,"E20.5.14.0"),sQuery(id+"F0.wireOp",EDGE,"E20.5.15.0"),sQuery(id+"F0.wireOp",EDGE,"E21.0.0.16"),sQuery(id+"F0.wireOp",EDGE,"E21.0.1.16"),sQuery(id+"F0.wireOp",EDGE,"E21.0.2.16"),sQuery(id+"F0.wireOp",EDGE,"E21.0.3.16"),sQuery(id+"F0.wireOp",EDGE,"E21.0.4.16"),sQuery(id+"F0.wireOp",EDGE,"E21.0.5.16"),sQuery(id+"F0.wireOp",EDGE,"E22"),sQuery(id+"F0.wireOp",EDGE,"E23.1.0.0"),sQuery(id+"F0.wireOp",EDGE,"E23.2.0.0"),sQuery(id+"F0.wireOp",EDGE,"E23.3.0.0"),sQuery(id+"F0.wireOp",EDGE,"E23.4.0.0"),sQuery(id+"F0.wireOp",EDGE,"E23.5.0.0")])],"isStart":false});
            var sketch = newSketch(context, id + "F4", { "sketchPlane" : qUnion([Q0])});
            skLineSegment(sketch, "E124.bottom", {"start": v(444.79, -1527.65) * mm, "end": v(646.4, -1527.65) * mm});
            skLineSegment(sketch, "E124.top", {"start": v(444.79, -1827.7) * mm, "end": v(646.4, -1827.7) * mm});
            skLineSegment(sketch, "E124.left", {"start": v(419.39, -1553.05) * mm, "end": v(419.39, -1802.3) * mm});
            skLineSegment(sketch, "E124.right", {"start": v(671.8, -1553.05) * mm, "end": v(671.8, -1802.3) * mm});
            skLineSegment(sketch, "E125", {"start": v(545.6, -1527.65) * mm, "end": v(545.6, -1827.7) * mm, "construction": true});
            skPoint(sketch, "E126.visualSharp", {"position": v(419.39, -1527.65) * mm});
            skArc(sketch, "E126.filletArc", {"start": v(444.79, -1527.65) * mm, "mid": v(426.83, -1535.1) * mm, "end": v(419.39, -1553.05) * mm});
            skPoint(sketch, "E127.visualSharp", {"position": v(671.8, -1527.65) * mm});
            skArc(sketch, "E127.filletArc", {"start": v(671.8, -1553.05) * mm, "mid": v(664.36, -1535.1) * mm, "end": v(646.4, -1527.65) * mm});
            skPoint(sketch, "E128.visualSharp", {"position": v(671.8, -1827.7) * mm});
            skArc(sketch, "E128.filletArc", {"start": v(646.4, -1827.7) * mm, "mid": v(664.36, -1820.25) * mm, "end": v(671.8, -1802.3) * mm});
            skPoint(sketch, "E129.visualSharp", {"position": v(419.39, -1827.7) * mm});
            skArc(sketch, "E129.filletArc", {"start": v(419.39, -1802.3) * mm, "mid": v(426.83, -1820.25) * mm, "end": v(444.79, -1827.7) * mm});
            skLineSegment(sketch, "E130", {"start": v(419.39, -1677.67) * mm, "end": v(671.8, -1677.67) * mm, "construction": true});
            skSolve(sketch);
        }
        {
            var Q0;
            Q0 = qSketchRegion(id + "F4", true);
            extrude(context, id + "F5", {"entities" : qUnion([Q0]), "operationType" : NewBodyOperationType.REMOVE, "oppositeDirection" : true, "depth" : 6.35 * mm});
        }
        {
            var Q0;
            Q0=makeQuery(id+"F5.boolean.opBoolean","COPY",FACE,{"derivedFrom":makeQuery(id+"F5.opExtrude","CAP_FACE",FACE,{"disambiguationData":[OSD([sQuery(id+"F4.wireOp",EDGE,"E124.bottom"),sQuery(id+"F4.wireOp",EDGE,"E124.top"),sQuery(id+"F4.wireOp",EDGE,"E124.left"),sQuery(id+"F4.wireOp",EDGE,"E124.right"),sQuery(id+"F4.wireOp",EDGE,"E126.filletArc"),sQuery(id+"F4.wireOp",EDGE,"E127.filletArc"),sQuery(id+"F4.wireOp",EDGE,"E128.filletArc"),sQuery(id+"F4.wireOp",EDGE,"E129.filletArc")])],"isStart":false})});
            var sketch = newSketch(context, id + "F6", { "sketchPlane" : qUnion([Q0])});
            skLineSegment(sketch, "E131.0", {"start": v(432.09, -1553.05) * mm, "end": v(432.09, -1802.3) * mm});
            skArc(sketch, "E131.1", {"start": v(444.79, -1540.35) * mm, "mid": v(435.8, -1544.07) * mm, "end": v(432.09, -1553.05) * mm});
            skArc(sketch, "E131.2", {"start": v(432.09, -1802.3) * mm, "mid": v(435.8, -1811.27) * mm, "end": v(444.79, -1815) * mm});
            skLineSegment(sketch, "E131.3", {"start": v(646.4, -1540.35) * mm, "end": v(444.79, -1540.35) * mm});
            skLineSegment(sketch, "E131.4", {"start": v(444.79, -1815) * mm, "end": v(646.4, -1815) * mm});
            skArc(sketch, "E131.5", {"start": v(646.4, -1815) * mm, "mid": v(655.38, -1811.27) * mm, "end": v(659.1, -1802.3) * mm});
            skLineSegment(sketch, "E131.6", {"start": v(659.1, -1802.3) * mm, "end": v(659.1, -1553.05) * mm});
            skArc(sketch, "E131.7", {"start": v(659.1, -1553.05) * mm, "mid": v(655.38, -1544.07) * mm, "end": v(646.4, -1540.35) * mm});
            skSolve(sketch);
        }
        {
            var Q0;
            Q0 = qSketchRegion(id + "F6", true);
            extrude(context, id + "F7", {"entities" : qUnion([Q0]), "operationType" : NewBodyOperationType.REMOVE, "endBound" : BoundingType.THROUGH_ALL, "oppositeDirection" : true, "depth" : 25.4 * mm});
        }
        {
            var Q0;
            Q0=makeQuery(id+"F1.opExtrude","CAP_FACE",FACE,{"disambiguationData":[OSD([sQuery(id+"F0.wireOp",EDGE,"E84.bottom"),sQuery(id+"F0.wireOp",EDGE,"E84.top"),sQuery(id+"F0.wireOp",EDGE,"E84.left"),sQuery(id+"F0.wireOp",EDGE,"E84.right"),sQuery(id+"F0.wireOp",EDGE,"E85"),sQuery(id+"F0.wireOp",EDGE,"E86"),sQuery(id+"F0.wireOp",EDGE,"E87.0.1.0"),sQuery(id+"F0.wireOp",EDGE,"E87.0.2.0"),sQuery(id+"F0.wireOp",EDGE,"E87.0.3.0"),sQuery(id+"F0.wireOp",EDGE,"E87.0.4.0"),sQuery(id+"F0.wireOp",EDGE,"E87.1.0.0"),sQuery(id+"F0.wireOp",EDGE,"E87.1.1.0"),sQuery(id+"F0.wireOp",EDGE,"E87.1.2.0"),sQuery(id+"F0.wireOp",EDGE,"E87.1.3.0"),sQuery(id+"F0.wireOp",EDGE,"E88")])],"isStart":false});
            var sketch = newSketch(context, id + "F8", { "sketchPlane" : qUnion([Q0])});
            skLineSegment(sketch, "E132.bottom", {"start": v(978.46, -152.84) * mm, "end": v(1003.86, -152.84) * mm});
            skLineSegment(sketch, "E132.top", {"start": v(978.46, -784.67) * mm, "end": v(1003.86, -784.67) * mm});
            skLineSegment(sketch, "E132.left", {"start": v(978.46, -152.84) * mm, "end": v(978.46, -784.67) * mm});
            skLineSegment(sketch, "E132.right", {"start": v(1003.86, -152.84) * mm, "end": v(1003.86, -784.67) * mm});
            skLineSegment(sketch, "E133.bottom", {"start": v(978.46, -1350.13) * mm, "end": v(1003.86, -1350.13) * mm});
            skLineSegment(sketch, "E133.top", {"start": v(978.46, -1981.96) * mm, "end": v(1003.86, -1981.96) * mm});
            skLineSegment(sketch, "E133.left", {"start": v(978.46, -1350.13) * mm, "end": v(978.46, -1981.96) * mm});
            skLineSegment(sketch, "E133.right", {"start": v(1003.86, -1350.13) * mm, "end": v(1003.86, -1981.96) * mm});
            skSolve(sketch);
        }
        {
            var Q0;
            Q0 = qSketchRegion(id + "F8", true);
            extrude(context, id + "F9", {"entities" : qUnion([Q0]), "operationType" : NewBodyOperationType.REMOVE, "oppositeDirection" : true, "depth" : 1.59 * mm});
        }
        {
            var Q0;
            Q0=makeQuery(id+"F1.opExtrude","CAP_FACE",FACE,{"disambiguationData":[OSD([sQuery(id+"F0.wireOp",EDGE,"E98.bottom"),sQuery(id+"F0.wireOp",EDGE,"E98.top"),sQuery(id+"F0.wireOp",EDGE,"E98.left"),sQuery(id+"F0.wireOp",EDGE,"E98.right")])],"isStart":true});
            var sketch = newSketch(context, id + "F10", { "sketchPlane" : qUnion([Q0])});
            skLineSegment(sketch, "E134.bottom", {"start": v(4797.52, 1787.05) * mm, "end": v(4813.4, 1787.05) * mm});
            skLineSegment(sketch, "E134.top", {"start": v(4797.52, 1329.85) * mm, "end": v(4813.4, 1329.85) * mm});
            skLineSegment(sketch, "E134.left", {"start": v(4797.52, 1787.05) * mm, "end": v(4797.52, 1329.85) * mm});
            skLineSegment(sketch, "E134.right", {"start": v(4813.4, 1787.05) * mm, "end": v(4813.4, 1329.85) * mm});
            skSolve(sketch);
        }
        {
            var Q0;
            Q0 = qSketchRegion(id + "F10", true);
            extrude(context, id + "F11", {"entities" : qUnion([Q0]), "operationType" : NewBodyOperationType.REMOVE, "oppositeDirection" : true, "depth" : 6.35 * mm});
        }
        {
            var Q0;
            Q0=makeQuery(id+"F1.opExtrude","CAP_FACE",FACE,{"disambiguationData":[OSD([sQuery(id+"F0.wireOp",EDGE,"E97.bottom"),sQuery(id+"F0.wireOp",EDGE,"E97.top"),sQuery(id+"F0.wireOp",EDGE,"E97.left"),sQuery(id+"F0.wireOp",EDGE,"E97.right")])],"isStart":false});
            var sketch = newSketch(context, id + "F12", { "sketchPlane" : qUnion([Q0])});
            skLineSegment(sketch, "E135.bottom", {"start": v(4389.47, -1759.07) * mm, "end": v(4599.02, -1759.07) * mm});
            skLineSegment(sketch, "E135.top", {"start": v(4389.47, -2032.12) * mm, "end": v(4599.02, -2032.12) * mm});
            skLineSegment(sketch, "E135.left", {"start": v(4389.47, -1759.07) * mm, "end": v(4389.47, -2032.12) * mm});
            skLineSegment(sketch, "E135.right", {"start": v(4599.02, -1759.07) * mm, "end": v(4599.02, -2032.12) * mm});
            skLineSegment(sketch, "E136", {"start": v(4494.25, -1759.07) * mm, "end": v(4494.25, -2032.12) * mm, "construction": true});
            skLineSegment(sketch, "E137", {"start": v(4389.47, -1895.6) * mm, "end": v(4599.02, -1895.6) * mm, "construction": true});
            skSolve(sketch);
        }
        {
            var Q0;
            Q0 = qSketchRegion(id + "F12", true);
            extrude(context, id + "F13", {"entities" : qUnion([Q0]), "operationType" : NewBodyOperationType.REMOVE, "endBound" : BoundingType.THROUGH_ALL, "oppositeDirection" : true, "depth" : 25.4 * mm});
        }
    });
